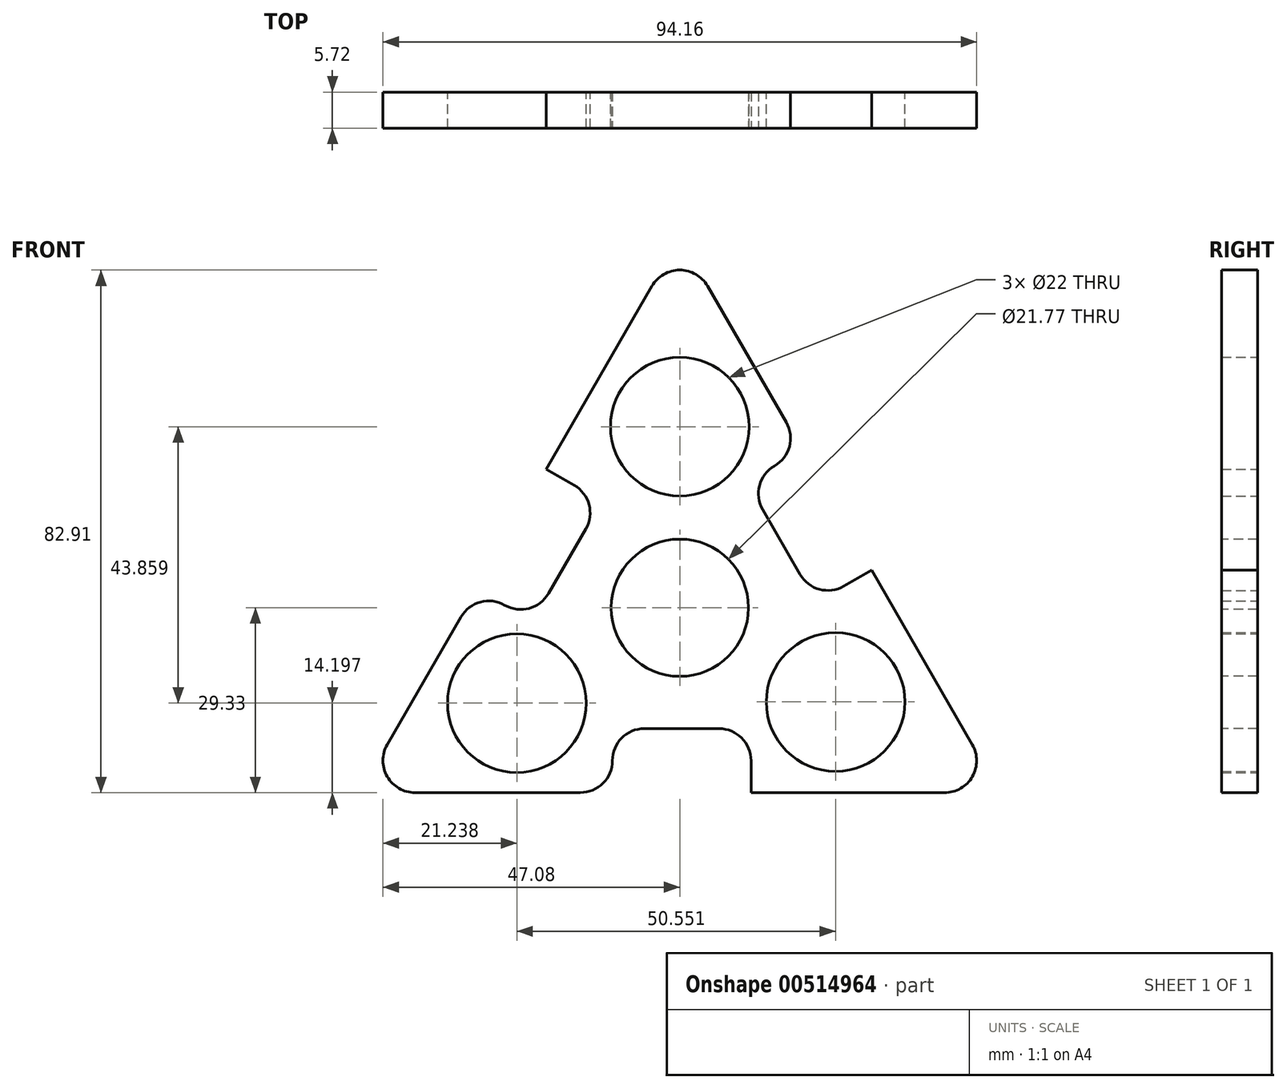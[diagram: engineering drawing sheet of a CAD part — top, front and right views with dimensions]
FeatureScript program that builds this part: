
annotation { "Feature Type Name" : "Feature", "Feature Type Description" : "" }
export const myFeature = defineFeature(function(context is Context, id is Id, definition is map)
    precondition{}
    {
        {
            var Q0;
            Q0=qCreatedBy(makeId("Front.planeOp"),FACE);
            var sketch = newSketch(context, id + "F0", { "sketchPlane" : qUnion([Q0])});
            skCircle(sketch, "E0.cCircle", {"center": v(0, 0) * mm, "radius": 29.33 * mm, "construction": true});
            skLineSegment(sketch, "E0.0", {"start": v(50.8, -29.33) * mm, "end": v(-50.8, -29.33) * mm});
            skLineSegment(sketch, "E0.1", {"start": v(-50.8, -29.33) * mm, "end": v(0, 58.66) * mm});
            skLineSegment(sketch, "E0.2", {"start": v(0, 58.66) * mm, "end": v(50.8, -29.33) * mm});
            skPoint(sketch, "E0.0.midPoint", {"position": v(0, -29.33) * mm});
            skSolve(sketch);
        }
        {
            var Q0;
            Q0=makeQuery(id+"F0.imprint","IMPRINT",FACE,{"disambiguationData":[TD([[makeQuery(id+"F0.imprint","IMPRINT",EDGE,{"derivedFrom":sQuery(id+"F0.wireOp",EDGE,"E0.0")}),-1.0]])]});
            extrude(context, id + "F1", {"entities" : qUnion([Q0]), "depth" : 5.7 * mm, "offsetDistance" : 25.4 * mm});
        }
        {
            var Q0;
            Q0=makeQuery(id+"F1.opExtrude","CAP_FACE",FACE,{"disambiguationData":[OSD([sQuery(id+"F0.wireOp",EDGE,"E0.0"),sQuery(id+"F0.wireOp",EDGE,"E0.1"),sQuery(id+"F0.wireOp",EDGE,"E0.2")])],"isStart":false});
            var sketch = newSketch(context, id + "F2", { "sketchPlane" : qUnion([Q0])});
            skCircle(sketch, "E1", {"center": v(0, 0) * mm, "radius": 10.88 * mm});
            skSolve(sketch);
        }
        {
            var Q0;
            Q0=makeQuery(id+"F2.imprint","IMPRINT",FACE,{"disambiguationData":[TD([[makeQuery(id+"F2.imprint","IMPRINT",EDGE,{"derivedFrom":sQuery(id+"F2.wireOp",EDGE,"E1")}),1.0]])]});
            extrude(context, id + "F3", {"entities" : qUnion([Q0]), "operationType" : NewBodyOperationType.REMOVE, "oppositeDirection" : true, "depth" : 25.4 * mm, "offsetDistance" : 25.4 * mm});
        }
        {
            var Q0;
            Q0=makeQuery(id+"F1.opExtrude","SWEPT_FACE",FACE,{"disambiguationData":[OSD([sQuery(id+"F0.wireOp",EDGE,"E0.2")])]});
            var sketch = newSketch(context, id + "F4", { "sketchPlane" : qUnion([Q0])});
            skLineSegment(sketch, "E2.bottom", {"start": v(-5.72, 11.96) * mm, "end": v(0, 11.96) * mm});
            skLineSegment(sketch, "E2.top", {"start": v(-5.72, -10.04) * mm, "end": v(0, -10.04) * mm});
            skLineSegment(sketch, "E2.left", {"start": v(-5.72, 11.96) * mm, "end": v(-5.72, -10.04) * mm});
            skLineSegment(sketch, "E2.right", {"start": v(0, 11.96) * mm, "end": v(0, -10.04) * mm});
            skSolve(sketch);
        }
        {
            var Q0;
            Q0 = qSketchRegion(id + "F4", true);
            extrude(context, id + "F5", {"entities" : qUnion([Q0]), "operationType" : NewBodyOperationType.REMOVE, "oppositeDirection" : true, "depth" : 10.16 * mm, "offsetDistance" : 25.4 * mm});
        }
        {
            var Q0;
            Q0=makeQuery(id+"F5.boolean.opBoolean","COPY",EDGE,{"derivedFrom":makeQuery(id+"F5.opExtrude","CAP_EDGE",EDGE,{"disambiguationData":[OSD([sQuery(id+"F4.wireOp",EDGE,"E2.top")])],"isStart":false})});
            var Q1;
            Q1=makeQuery(id+"F5.boolean.opBoolean","COPY",EDGE,{"derivedFrom":makeQuery(id+"F5.opExtrude","CAP_EDGE",EDGE,{"disambiguationData":[OSD([sQuery(id+"F4.wireOp",EDGE,"E2.bottom")])],"isStart":false})});
            var Q2;
            Q2=makeQuery(id+"F5.boolean.opBoolean","COPY",EDGE,{"derivedFrom":makeQuery(id+"F5.opExtrude","CAP_EDGE",EDGE,{"disambiguationData":[OSD([sQuery(id+"F4.wireOp",EDGE,"E2.top")])],"isStart":true})});
            var Q3;
            Q3=makeQuery(id+"F5.boolean.opBoolean","COPY",EDGE,{"derivedFrom":makeQuery(id+"F5.opExtrude","CAP_EDGE",EDGE,{"disambiguationData":[OSD([sQuery(id+"F4.wireOp",EDGE,"E2.bottom")])],"isStart":true})});
            fillet(context, id + "F6", {"entities" : qUnion([Q0, Q1, Q2, Q3]), "radius" : 5.08 * mm, "tangentPropagation" : true, "allowEdgeOverflow" : false});
        }
        {
            var Q0;
            Q0=makeQuery(id+"F1.opExtrude","SWEPT_EDGE",EDGE,{"disambiguationData":[OSD([sQuery(id+"F0.wireOp",EDGE,"E0.0"),sQuery(id+"F0.wireOp",EDGE,"E0.2")])]});
            var Q1;
            Q1=makeQuery(id+"F1.opExtrude","SWEPT_EDGE",EDGE,{"disambiguationData":[OSD([sQuery(id+"F0.wireOp",EDGE,"E0.0"),sQuery(id+"F0.wireOp",EDGE,"E0.1")])]});
            var Q2;
            Q2=makeQuery(id+"F1.opExtrude","SWEPT_EDGE",EDGE,{"disambiguationData":[OSD([sQuery(id+"F0.wireOp",EDGE,"E0.1"),sQuery(id+"F0.wireOp",EDGE,"E0.2")])]});
            fillet(context, id + "F7", {"entities" : qUnion([Q0, Q1, Q2]), "radius" : 5.08 * mm, "tangentPropagation" : true, "allowEdgeOverflow" : false});
        }
        {
            var Q0;
            Q0=makeQuery(id+"F1.opExtrude","SWEPT_FACE",FACE,{"disambiguationData":[OSD([sQuery(id+"F0.wireOp",EDGE,"E0.1")])]});
            var sketch = newSketch(context, id + "F8", { "sketchPlane" : qUnion([Q0])});
            skLineSegment(sketch, "E3.bottom", {"start": v(5.72, 8.46) * mm, "end": v(0, 8.46) * mm});
            skLineSegment(sketch, "E3.top", {"start": v(5.72, -13.53) * mm, "end": v(0, -13.53) * mm});
            skLineSegment(sketch, "E3.left", {"start": v(5.72, 8.46) * mm, "end": v(5.72, -13.53) * mm});
            skLineSegment(sketch, "E3.right", {"start": v(0, 8.46) * mm, "end": v(0, -13.53) * mm});
            skSolve(sketch);
        }
        {
            var Q0;
            Q0 = qSketchRegion(id + "F8", true);
            extrude(context, id + "F9", {"entities" : qUnion([Q0]), "operationType" : NewBodyOperationType.REMOVE, "oppositeDirection" : true, "depth" : 10.16 * mm, "offsetDistance" : 25.4 * mm});
        }
        {
            var Q0;
            Q0=makeQuery(id+"F9.boolean.opBoolean","COPY",EDGE,{"derivedFrom":makeQuery(id+"F9.opExtrude","CAP_EDGE",EDGE,{"disambiguationData":[OSD([sQuery(id+"F8.wireOp",EDGE,"E3.bottom")])],"isStart":true})});
            var Q1;
            Q1=makeQuery(id+"F9.boolean.opBoolean","COPY",EDGE,{"derivedFrom":makeQuery(id+"F9.opExtrude","CAP_EDGE",EDGE,{"disambiguationData":[OSD([sQuery(id+"F8.wireOp",EDGE,"E3.bottom")])],"isStart":false})});
            var Q2;
            Q2=makeQuery(id+"F9.boolean.opBoolean","COPY",EDGE,{"derivedFrom":makeQuery(id+"F9.opExtrude","CAP_EDGE",EDGE,{"disambiguationData":[OSD([sQuery(id+"F8.wireOp",EDGE,"E3.top")])],"isStart":true})});
            var Q3;
            Q3=makeQuery(id+"F9.boolean.opBoolean","COPY",EDGE,{"derivedFrom":makeQuery(id+"F9.opExtrude","CAP_EDGE",EDGE,{"disambiguationData":[OSD([sQuery(id+"F8.wireOp",EDGE,"E3.top")])],"isStart":false})});
            fillet(context, id + "F10", {"entities" : qUnion([Q0, Q1, Q2, Q3]), "radius" : 5.08 * mm, "tangentPropagation" : true, "allowEdgeOverflow" : false});
        }
        {
            var Q0;
            Q0=makeQuery(id+"F1.opExtrude","SWEPT_FACE",FACE,{"disambiguationData":[OSD([sQuery(id+"F0.wireOp",EDGE,"E0.0")])]});
            var sketch = newSketch(context, id + "F11", { "sketchPlane" : qUnion([Q0])});
            skLineSegment(sketch, "E4.bottom", {"start": v(11.3, 0) * mm, "end": v(-10.7, 0) * mm});
            skLineSegment(sketch, "E4.top", {"start": v(11.3, 5.72) * mm, "end": v(-10.7, 5.72) * mm});
            skLineSegment(sketch, "E4.left", {"start": v(11.3, 0) * mm, "end": v(11.3, 5.72) * mm});
            skLineSegment(sketch, "E4.right", {"start": v(-10.7, 0) * mm, "end": v(-10.7, 5.72) * mm});
            skSolve(sketch);
        }
        {
            var Q0;
            Q0 = qSketchRegion(id + "F11", true);
            extrude(context, id + "F12", {"entities" : qUnion([Q0]), "operationType" : NewBodyOperationType.REMOVE, "oppositeDirection" : true, "depth" : 10.16 * mm, "offsetDistance" : 25.4 * mm});
        }
        {
            var Q0;
            Q0=makeQuery(id+"F12.boolean.opBoolean","COPY",EDGE,{"derivedFrom":makeQuery(id+"F12.opExtrude","CAP_EDGE",EDGE,{"disambiguationData":[OSD([sQuery(id+"F11.wireOp",EDGE,"E4.left")])],"isStart":true})});
            var Q1;
            Q1=makeQuery(id+"F12.boolean.opBoolean","COPY",EDGE,{"derivedFrom":makeQuery(id+"F12.opExtrude","CAP_EDGE",EDGE,{"disambiguationData":[OSD([sQuery(id+"F11.wireOp",EDGE,"E4.left")])],"isStart":false})});
            var Q2;
            Q2=makeQuery(id+"F12.boolean.opBoolean","COPY",EDGE,{"derivedFrom":makeQuery(id+"F12.opExtrude","CAP_EDGE",EDGE,{"disambiguationData":[OSD([sQuery(id+"F11.wireOp",EDGE,"E4.right")])],"isStart":true})});
            var Q3;
            Q3=makeQuery(id+"F12.boolean.opBoolean","COPY",EDGE,{"derivedFrom":makeQuery(id+"F12.opExtrude","CAP_EDGE",EDGE,{"disambiguationData":[OSD([sQuery(id+"F11.wireOp",EDGE,"E4.right")])],"isStart":false})});
            fillet(context, id + "F13", {"entities" : qUnion([Q0, Q1, Q2, Q3]), "radius" : 5.08 * mm, "tangentPropagation" : true, "allowEdgeOverflow" : false});
        }
        {
            var Q0;
            Q0=makeQuery(id+"F1.opExtrude","CAP_FACE",FACE,{"disambiguationData":[OSD([sQuery(id+"F0.wireOp",EDGE,"E0.0"),sQuery(id+"F0.wireOp",EDGE,"E0.1"),sQuery(id+"F0.wireOp",EDGE,"E0.2")])],"isStart":true});
            var sketch = newSketch(context, id + "F14", { "sketchPlane" : qUnion([Q0])});
            skCircle(sketch, "E5", {"center": v(0, 28.73) * mm, "radius": 11 * mm});
            skCircle(sketch, "E6", {"center": v(25.84, -15.13) * mm, "radius": 11 * mm});
            skCircle(sketch, "E7", {"center": v(-24.7, -14.94) * mm, "radius": 11 * mm});
            skSolve(sketch);
        }
        {
            var Q0;
            Q0=makeQuery(id+"F14.imprint","IMPRINT",FACE,{"disambiguationData":[TD([[makeQuery(id+"F14.imprint","IMPRINT",EDGE,{"derivedFrom":sQuery(id+"F14.wireOp",EDGE,"E5")}),1.0]])]});
            var Q1;
            Q1=makeQuery(id+"F14.imprint","IMPRINT",FACE,{"disambiguationData":[TD([[makeQuery(id+"F14.imprint","IMPRINT",EDGE,{"derivedFrom":sQuery(id+"F14.wireOp",EDGE,"E6")}),1.0]])]});
            var Q2;
            Q2=makeQuery(id+"F14.imprint","IMPRINT",FACE,{"disambiguationData":[TD([[makeQuery(id+"F14.imprint","IMPRINT",EDGE,{"derivedFrom":sQuery(id+"F14.wireOp",EDGE,"E7")}),1.0]])]});
            extrude(context, id + "F15", {"entities" : qUnion([Q0, Q1, Q2]), "operationType" : NewBodyOperationType.REMOVE, "oppositeDirection" : true, "depth" : 25.4 * mm, "offsetDistance" : 25.4 * mm});
        }
    });
